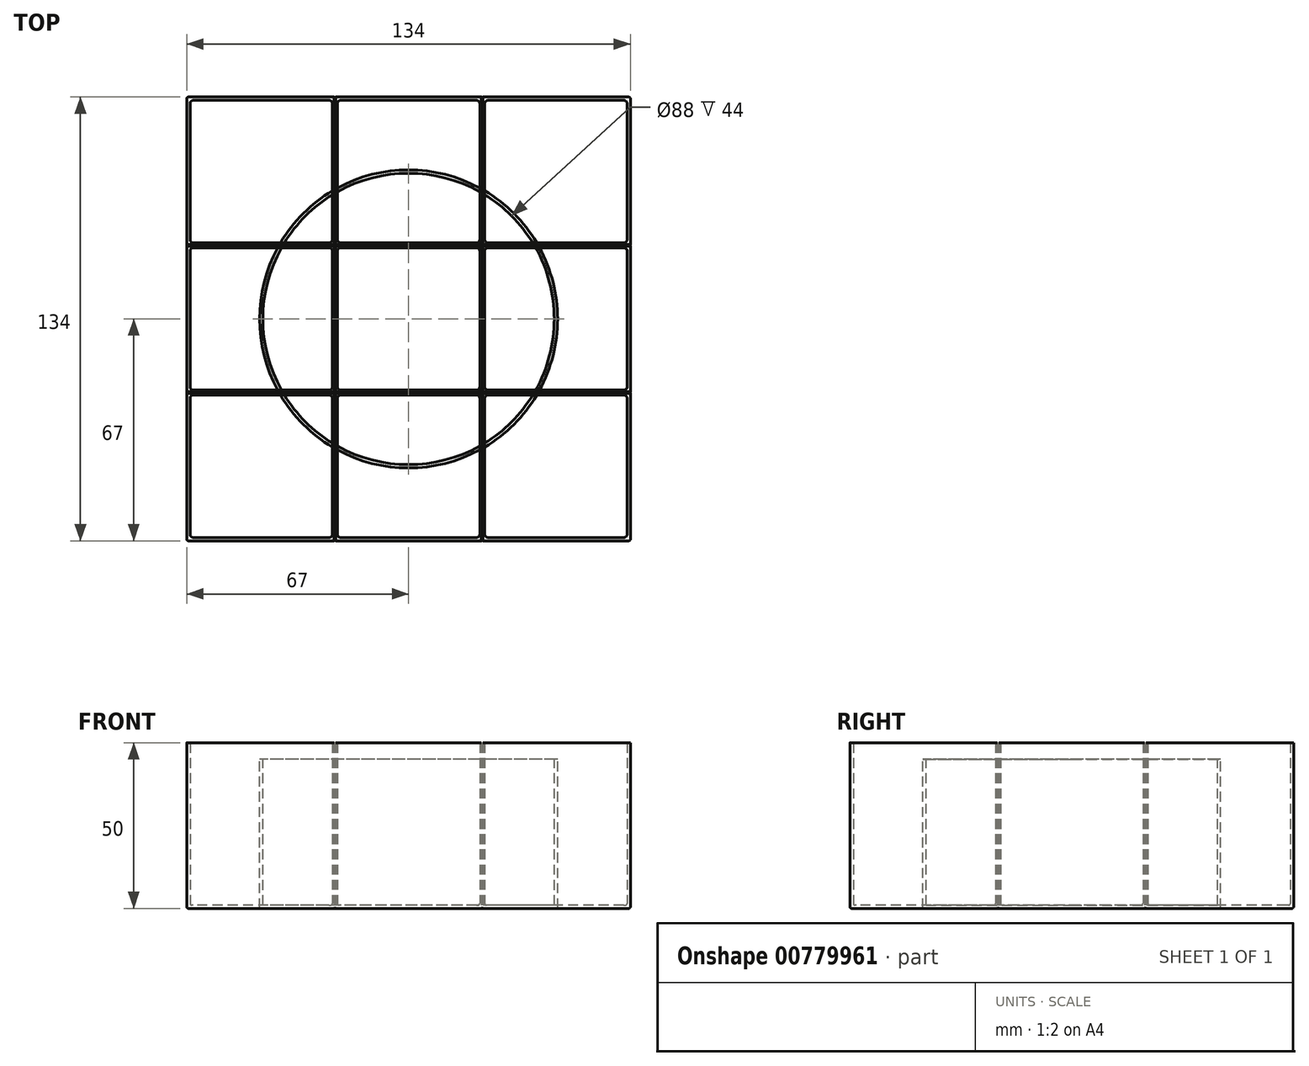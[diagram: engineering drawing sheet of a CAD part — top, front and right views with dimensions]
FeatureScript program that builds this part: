
annotation { "Feature Type Name" : "Feature", "Feature Type Description" : "" }
export const myFeature = defineFeature(function(context is Context, id is Id, definition is map)
    precondition{}
    {
        {
            var Q0;
            Q0=qCreatedBy(makeId("Front.planeOp"),FACE);
            var sketch = newSketch(context, id + "F0", { "sketchPlane" : qUnion([Q0])});
            skLineSegment(sketch, "E0.bottom", {"start": v(0, 0) * mm, "end": v(-45, 0) * mm});
            skLineSegment(sketch, "E0.top", {"start": v(0, 45) * mm, "end": v(-45, 45) * mm});
            skLineSegment(sketch, "E0.left", {"start": v(0, 0) * mm, "end": v(0, 45) * mm});
            skLineSegment(sketch, "E0.right", {"start": v(-45, 0) * mm, "end": v(-45, 45) * mm});
            skLineSegment(sketch, "E1.bottom", {"start": v(0, 45) * mm, "end": v(-44, 45) * mm});
            skLineSegment(sketch, "E1.top", {"start": v(0, 1) * mm, "end": v(-44, 1) * mm});
            skLineSegment(sketch, "E1.left", {"start": v(0, 45) * mm, "end": v(0, 1) * mm});
            skLineSegment(sketch, "E1.right", {"start": v(-44, 45) * mm, "end": v(-44, 1) * mm});
            skSolve(sketch);
        }
        {
            var Q0;
            Q0=makeQuery(id+"F0.imprint","IMPRINT",FACE,{"disambiguationData":[TD([[makeQuery(id+"F0.imprint","IMPRINT",EDGE,{"derivedFrom":sQuery(id+"F0.wireOp",EDGE,"E0.bottom")}),-1.0]])]});
            var Q1;
            Q1=sQuery(id+"F0.wireOp",EDGE,"E1.left");
            revolve(context, id + "F1", {"surfaceOperationType" : NewSurfaceOperationType.NEW, "entities" : qUnion([Q0]), "axis" : qUnion([Q1]), "revolveType" : RevolveType.FULL});
        }
        {
            var Q0;
            Q0=qCreatedBy(makeId("Top.planeOp"),FACE);
            var sketch = newSketch(context, id + "F2", { "sketchPlane" : qUnion([Q0])});
            skLineSegment(sketch, "E2.bottom", {"start": v(22.5, 22.5) * mm, "end": v(-22.5, 22.5) * mm});
            skLineSegment(sketch, "E2.top", {"start": v(22.5, -22.5) * mm, "end": v(-22.5, -22.5) * mm});
            skLineSegment(sketch, "E2.left", {"start": v(22.5, 22.5) * mm, "end": v(22.5, -22.5) * mm});
            skLineSegment(sketch, "E2.right", {"start": v(-22.5, 22.5) * mm, "end": v(-22.5, -22.5) * mm});
            skPoint(sketch, "E2.middle", {"position": v(0, 0) * mm});
            skSolve(sketch);
        }
        {
            var Q0;
            Q0 = qSketchRegion(id + "F2", true);
            extrude(context, id + "F3", {"entities" : qUnion([Q0]), "depth" : 50 * mm, "offsetDistance" : 25 * mm});
        }
        {
            var Q0;
            Q0=makeQuery(id+"F3.opExtrude","CAP_FACE",FACE,{"disambiguationData":[OSD([sQuery(id+"F2.wireOp",EDGE,"E2.bottom"),sQuery(id+"F2.wireOp",EDGE,"E2.top"),sQuery(id+"F2.wireOp",EDGE,"E2.left"),sQuery(id+"F2.wireOp",EDGE,"E2.right")])],"isStart":false});
            shell(context, id + "F4", {"entities" : qUnion([Q0]), "thickness" : 1 * mm});
        }
        {
            var Q0;
            Q0=makeQuery(id+"F3.opExtrude","SWEPT_EDGE",EDGE,{"disambiguationData":[OSD([sQuery(id+"F2.wireOp",EDGE,"E2.bottom"),sQuery(id+"F2.wireOp",EDGE,"E2.left")])]});
            var Q1;
            Q1=makeQuery(id+"F3.opExtrude","SWEPT_EDGE",EDGE,{"disambiguationData":[OSD([sQuery(id+"F2.wireOp",EDGE,"E2.bottom"),sQuery(id+"F2.wireOp",EDGE,"E2.right")])]});
            var Q2;
            Q2=makeQuery(id+"F3.opExtrude","SWEPT_EDGE",EDGE,{"disambiguationData":[OSD([sQuery(id+"F2.wireOp",EDGE,"E2.top"),sQuery(id+"F2.wireOp",EDGE,"E2.right")])]});
            var Q3;
            Q3=makeQuery(id+"F3.opExtrude","SWEPT_EDGE",EDGE,{"disambiguationData":[OSD([sQuery(id+"F2.wireOp",EDGE,"E2.top"),sQuery(id+"F2.wireOp",EDGE,"E2.left")])]});
            fillet(context, id + "F5", {"entities" : qUnion([Q0, Q1, Q2, Q3]), "radius" : .5 * mm, "tangentPropagation" : true, "allowEdgeOverflow" : false});
        }
        {
            var Q0;
            Q0=makeQuery(id+"F3.opExtrude","CAP_FACE",FACE,{"disambiguationData":[OSD([sQuery(id+"F2.wireOp",EDGE,"E2.bottom"),sQuery(id+"F2.wireOp",EDGE,"E2.top"),sQuery(id+"F2.wireOp",EDGE,"E2.left"),sQuery(id+"F2.wireOp",EDGE,"E2.right")])],"isStart":true});
            fillet(context, id + "F6", {"entities" : qUnion([Q0]), "radius" : .5 * mm, "tangentPropagation" : true, "allowEdgeOverflow" : false});
        }
        {
            var Q0;
            Q0=makeQuery(id+"F4.opShell","OFFSET_FACE",FACE,{"disambiguationData":[OSD([sQuery(id+"F2.wireOp",EDGE,"E2.bottom"),sQuery(id+"F2.wireOp",EDGE,"E2.top"),sQuery(id+"F2.wireOp",EDGE,"E2.left"),sQuery(id+"F2.wireOp",EDGE,"E2.right")])]});
            fillet(context, id + "F7", {"entities" : qUnion([Q0]), "radius" : .5 * mm, "tangentPropagation" : true, "allowEdgeOverflow" : false});
        }
        {
            var Q0;
            Q0=makeQuery(id+"F4.opShell","OFFSET_EDGE",EDGE,{"disambiguationData":[OSD([sQuery(id+"F2.wireOp",EDGE,"E2.bottom"),sQuery(id+"F2.wireOp",EDGE,"E2.right")])]});
            var Q1;
            Q1=makeQuery(id+"F4.opShell","OFFSET_EDGE",EDGE,{"disambiguationData":[OSD([sQuery(id+"F2.wireOp",EDGE,"E2.top"),sQuery(id+"F2.wireOp",EDGE,"E2.right")])]});
            var Q2;
            Q2=makeQuery(id+"F4.opShell","OFFSET_EDGE",EDGE,{"disambiguationData":[OSD([sQuery(id+"F2.wireOp",EDGE,"E2.bottom"),sQuery(id+"F2.wireOp",EDGE,"E2.left")])]});
            var Q3;
            Q3=makeQuery(id+"F4.opShell","OFFSET_EDGE",EDGE,{"disambiguationData":[OSD([sQuery(id+"F2.wireOp",EDGE,"E2.top"),sQuery(id+"F2.wireOp",EDGE,"E2.left")])]});
            fillet(context, id + "F8", {"entities" : qUnion([Q0, Q1, Q2, Q3]), "radius" : 1 * mm, "tangentPropagation" : true, "allowEdgeOverflow" : false});
        }
        {
            var Q0;
            Q0=makeQuery(id+"F3.opExtrude","SWEPT_BODY",BODY,{"disambiguationData":[OSD([sQuery(id+"F2.wireOp",EDGE,"E2.bottom"),sQuery(id+"F2.wireOp",EDGE,"E2.top"),sQuery(id+"F2.wireOp",EDGE,"E2.left"),sQuery(id+"F2.wireOp",EDGE,"E2.right")])]});
            transform(context, id + "F9", {"entities" : qUnion([Q0]), "transformType" : TransformType.TRANSLATION_3D, "dx" : 0 * mm, "dy" : -44.5 * mm, "dz" : 0 * mm, "makeCopy" : true});
        }
        {
            var Q0;
            Q0=makeQuery(id+"F9.opPattern","COPY",BODY,{"derivedFrom":makeQuery(id+"F3.opExtrude","SWEPT_BODY",BODY,{"disambiguationData":[OSD([sQuery(id+"F2.wireOp",EDGE,"E2.bottom"),sQuery(id+"F2.wireOp",EDGE,"E2.top"),sQuery(id+"F2.wireOp",EDGE,"E2.left"),sQuery(id+"F2.wireOp",EDGE,"E2.right")])]}),"instanceName":"1"});
            transform(context, id + "F10", {"entities" : qUnion([Q0]), "transformType" : TransformType.TRANSLATION_3D, "dx" : -44.5 * mm, "dy" : 0 * mm, "dz" : 0 * mm, "makeCopy" : true});
        }
        {
            var Q0;
            Q0=makeQuery(id+"F3.opExtrude","SWEPT_BODY",BODY,{"disambiguationData":[OSD([sQuery(id+"F2.wireOp",EDGE,"E2.bottom"),sQuery(id+"F2.wireOp",EDGE,"E2.top"),sQuery(id+"F2.wireOp",EDGE,"E2.left"),sQuery(id+"F2.wireOp",EDGE,"E2.right")])]});
            transform(context, id + "F11", {"entities" : qUnion([Q0]), "transformType" : TransformType.TRANSLATION_3D, "dx" : -44.5 * mm, "dy" : 0 * mm, "dz" : 0 * mm, "makeCopy" : true});
        }
        {
            var Q0;
            Q0=makeQuery(id+"F11.opPattern","COPY",BODY,{"derivedFrom":makeQuery(id+"F3.opExtrude","SWEPT_BODY",BODY,{"disambiguationData":[OSD([sQuery(id+"F2.wireOp",EDGE,"E2.bottom"),sQuery(id+"F2.wireOp",EDGE,"E2.top"),sQuery(id+"F2.wireOp",EDGE,"E2.left"),sQuery(id+"F2.wireOp",EDGE,"E2.right")])]}),"instanceName":"1"});
            transform(context, id + "F12", {"entities" : qUnion([Q0]), "transformType" : TransformType.TRANSLATION_3D, "dx" : 0 * mm, "dy" : 44.5 * mm, "dz" : 0 * mm, "makeCopy" : true});
        }
        {
            var Q0;
            Q0=makeQuery(id+"F3.opExtrude","SWEPT_BODY",BODY,{"disambiguationData":[OSD([sQuery(id+"F2.wireOp",EDGE,"E2.bottom"),sQuery(id+"F2.wireOp",EDGE,"E2.top"),sQuery(id+"F2.wireOp",EDGE,"E2.left"),sQuery(id+"F2.wireOp",EDGE,"E2.right")])]});
            transform(context, id + "F13", {"entities" : qUnion([Q0]), "transformType" : TransformType.TRANSLATION_3D, "dx" : 0 * mm, "dy" : 44.5 * mm, "dz" : 0 * mm, "makeCopy" : true});
        }
        {
            var Q0;
            Q0=makeQuery(id+"F3.opExtrude","SWEPT_BODY",BODY,{"disambiguationData":[OSD([sQuery(id+"F2.wireOp",EDGE,"E2.bottom"),sQuery(id+"F2.wireOp",EDGE,"E2.top"),sQuery(id+"F2.wireOp",EDGE,"E2.left"),sQuery(id+"F2.wireOp",EDGE,"E2.right")])]});
            transform(context, id + "F14", {"entities" : qUnion([Q0]), "transformType" : TransformType.TRANSLATION_3D, "dx" : 44.5 * mm, "dy" : 0 * mm, "dz" : 0 * mm, "makeCopy" : true});
        }
        {
            var Q0;
            Q0=makeQuery(id+"F9.opPattern","COPY",BODY,{"derivedFrom":makeQuery(id+"F3.opExtrude","SWEPT_BODY",BODY,{"disambiguationData":[OSD([sQuery(id+"F2.wireOp",EDGE,"E2.bottom"),sQuery(id+"F2.wireOp",EDGE,"E2.top"),sQuery(id+"F2.wireOp",EDGE,"E2.left"),sQuery(id+"F2.wireOp",EDGE,"E2.right")])]}),"instanceName":"1"});
            transform(context, id + "F15", {"entities" : qUnion([Q0]), "transformType" : TransformType.TRANSLATION_3D, "dx" : 44.5 * mm, "dy" : 0 * mm, "dz" : 0 * mm, "makeCopy" : true});
        }
        {
            var Q0;
            Q0=makeQuery(id+"F13.opPattern","COPY",BODY,{"derivedFrom":makeQuery(id+"F3.opExtrude","SWEPT_BODY",BODY,{"disambiguationData":[OSD([sQuery(id+"F2.wireOp",EDGE,"E2.bottom"),sQuery(id+"F2.wireOp",EDGE,"E2.top"),sQuery(id+"F2.wireOp",EDGE,"E2.left"),sQuery(id+"F2.wireOp",EDGE,"E2.right")])]}),"instanceName":"1"});
            transform(context, id + "F16", {"entities" : qUnion([Q0]), "transformType" : TransformType.TRANSLATION_3D, "dx" : 44.5 * mm, "dy" : 0 * mm, "dz" : 0 * mm, "makeCopy" : true});
        }
    });
